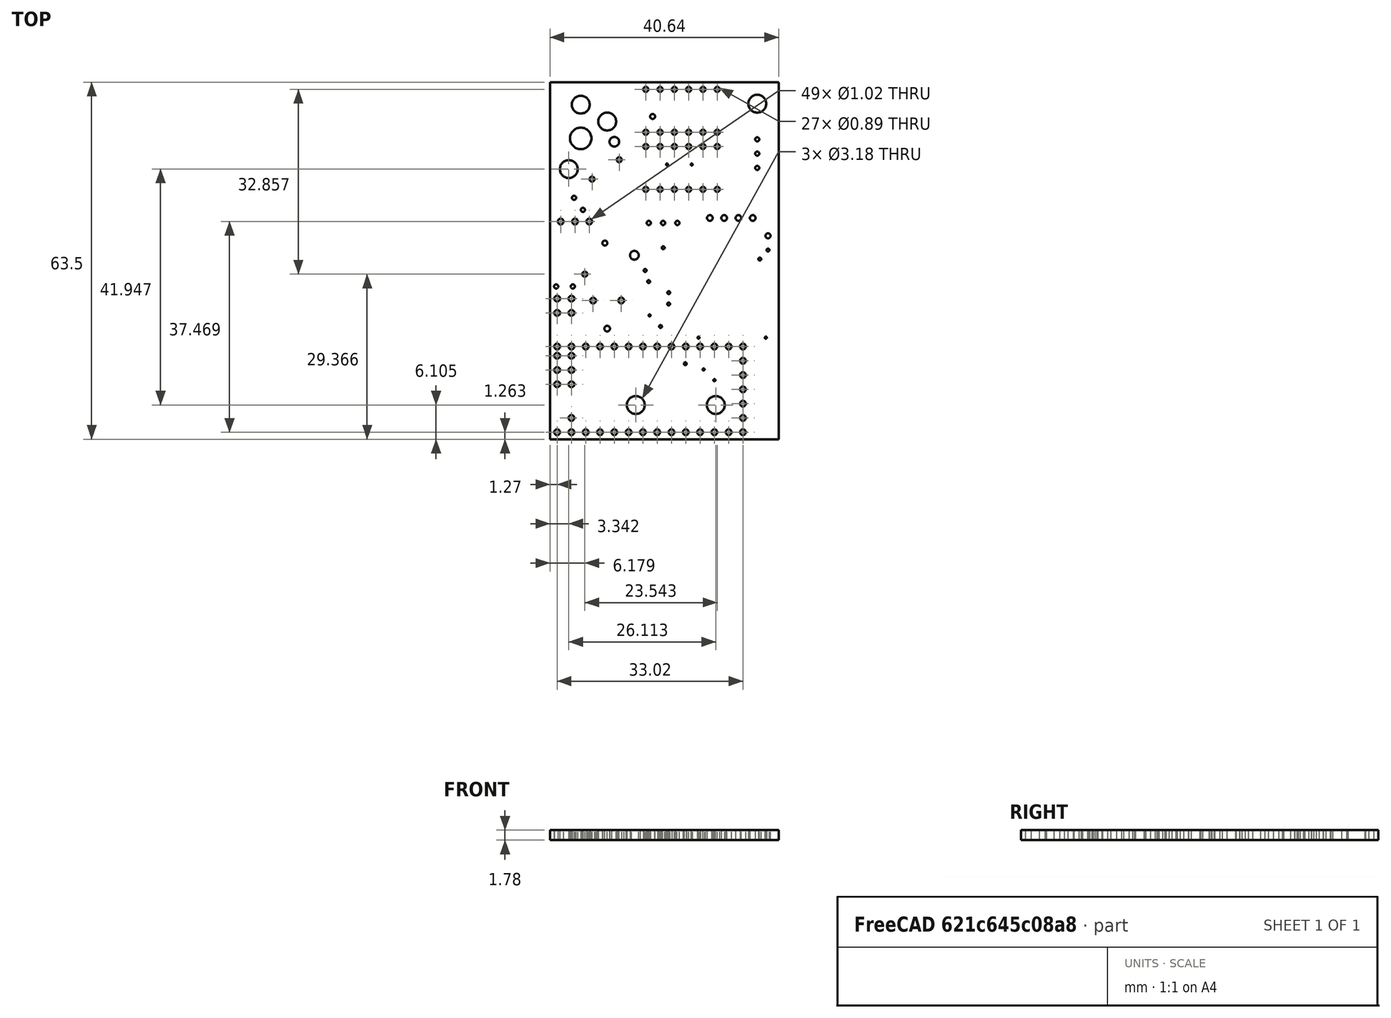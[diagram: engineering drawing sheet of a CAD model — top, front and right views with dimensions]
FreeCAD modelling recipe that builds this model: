
FCSTD DOCUMENT  (FreeCAD 1.0R39109 (Git))
Label: Version2PCB
License: All rights reserved
LicenseURL: https://en.wikipedia.org/wiki/All_rights_reserved
objects: Sketcher::SketchObject×2, PartDesign::Pad×1, PartDesign::Pocket×1, PartDesign::Body×1
note: 11 computed .brp shape members not serialized (recipe doc carries the construction recipe); baked Part::Feature solids carry a one-line shape summary decoded from their .brp

FEATURE [Sketcher::SketchObject] MainSketch
  ArcFitTolerance = 1e-06
  AttachmentSupport = -> [XY_Plane]
  FullyConstrained = false
  MakeInternals = false
  MapMode = 5
  sketch-geometry (4):
    g0: LineSegment StartX=0 StartY=0 StartZ=0 EndX=40.64 EndY=0 EndZ=0
    g1: LineSegment StartX=40.64 StartY=0 StartZ=0 EndX=40.64 EndY=63.5 EndZ=0
    g2: LineSegment StartX=40.64 StartY=63.5 StartZ=0 EndX=0 EndY=63.5 EndZ=0
    g3: LineSegment StartX=0 StartY=63.5 StartZ=0 EndX=0 EndY=0 EndZ=0
  constraints (4):
    c: Horizontal(g0)
    c: Horizontal(g2)
    c: Vertical(g1)
    c: Vertical(g3)
FEATURE [PartDesign::Pad] Main
  Direction = (0,0,1)
  Length = 1.778
  Length2 = 100.076
  Profile = -> MainSketch
  Refine = true
  Suppressed = false
  Type = 0
FEATURE [Sketcher::SketchObject] HoleSketch
  ArcFitTolerance = 1e-06
  AttachmentSupport = -> [XY_Plane]
  FullyConstrained = false
  MakeInternals = false
  MapMode = 5
  sketch-geometry (119):
    g0: Circle CenterX=5.4662 CenterY=59.5118 CenterZ=0 NormalX=0 NormalY=0 NormalZ=1 AngleXU=0 Radius=1.58564
    g1: Circle CenterX=5.45877 CenterY=53.5108 CenterZ=0 NormalX=0 NormalY=0 NormalZ=1 AngleXU=0 Radius=1.90871
    g2: Circle CenterX=10.16 CenterY=56.5113 CenterZ=0 NormalX=0 NormalY=0 NormalZ=1 AngleXU=0 Radius=1.58564
    g3: Circle CenterX=37.283 CenterY=32.0396 CenterZ=0 NormalX=0 NormalY=0 NormalZ=1 AngleXU=0 Radius=0.252515
    g4: Circle CenterX=19.6516 CenterY=20.0675 CenterZ=0 NormalX=0 NormalY=0 NormalZ=1 AngleXU=0 Radius=0.252515
    g5: Circle CenterX=38.7387 CenterY=33.6661 CenterZ=0 NormalX=0 NormalY=0 NormalZ=1 AngleXU=0 Radius=0.256228
    g6: Circle CenterX=20.1195 CenterY=34.0598 CenterZ=0 NormalX=0 NormalY=0 NormalZ=1 AngleXU=0 Radius=0.256228
    g7: Circle CenterX=21.1073 CenterY=26.0833 CenterZ=0 NormalX=0 NormalY=0 NormalZ=1 AngleXU=0 Radius=0.252515
    g8: Circle CenterX=21.0775 CenterY=24.0632 CenterZ=0 NormalX=0 NormalY=0 NormalZ=1 AngleXU=0 Radius=0.252515
    g9: Circle CenterX=17.0225 CenterY=62.2226 CenterZ=0 NormalX=0 NormalY=0 NormalZ=1 AngleXU=0 Radius=0.445614
    g10: Circle CenterX=17.0225 CenterY=54.6026 CenterZ=0 NormalX=0 NormalY=0 NormalZ=1 AngleXU=0 Radius=0.445614
    g11: Circle CenterX=19.5625 CenterY=62.2226 CenterZ=0 NormalX=0 NormalY=0 NormalZ=1 AngleXU=0 Radius=0.445614
    g12: Circle CenterX=19.5625 CenterY=54.6026 CenterZ=0 NormalX=0 NormalY=0 NormalZ=1 AngleXU=0 Radius=0.445614
    g13: Circle CenterX=22.1025 CenterY=62.2226 CenterZ=0 NormalX=0 NormalY=0 NormalZ=1 AngleXU=0 Radius=0.445614
    g14: Circle CenterX=22.1025 CenterY=54.6026 CenterZ=0 NormalX=0 NormalY=0 NormalZ=1 AngleXU=0 Radius=0.445614
    g15: Circle CenterX=24.6425 CenterY=62.2226 CenterZ=0 NormalX=0 NormalY=0 NormalZ=1 AngleXU=0 Radius=0.445614
    g16: Circle CenterX=24.6425 CenterY=54.6026 CenterZ=0 NormalX=0 NormalY=0 NormalZ=1 AngleXU=0 Radius=0.445614
    g17: Circle CenterX=27.1825 CenterY=62.2226 CenterZ=0 NormalX=0 NormalY=0 NormalZ=1 AngleXU=0 Radius=0.445614
    g18: Circle CenterX=29.7225 CenterY=62.2226 CenterZ=0 NormalX=0 NormalY=0 NormalZ=1 AngleXU=0 Radius=0.445614
    g19: Circle CenterX=27.1825 CenterY=54.6026 CenterZ=0 NormalX=0 NormalY=0 NormalZ=1 AngleXU=0 Radius=0.445614
    g20: Circle CenterX=29.7225 CenterY=54.6026 CenterZ=0 NormalX=0 NormalY=0 NormalZ=1 AngleXU=0 Radius=0.445614
    g21: Circle CenterX=34.29 CenterY=1.26257 CenterZ=0 NormalX=0 NormalY=0 NormalZ=1 AngleXU=0 Radius=0.508743
    g22: Circle CenterX=31.75 CenterY=1.26257 CenterZ=0 NormalX=0 NormalY=0 NormalZ=1 AngleXU=0 Radius=0.508743
    g23: Circle CenterX=29.21 CenterY=1.26257 CenterZ=0 NormalX=0 NormalY=0 NormalZ=1 AngleXU=0 Radius=0.508743
    g24: Circle CenterX=34.29 CenterY=16.5026 CenterZ=0 NormalX=0 NormalY=0 NormalZ=1 AngleXU=0 Radius=0.508743
    g25: Circle CenterX=34.29 CenterY=3.80257 CenterZ=0 NormalX=0 NormalY=0 NormalZ=1 AngleXU=0 Radius=0.508743
    g26: Circle CenterX=34.29 CenterY=6.34257 CenterZ=0 NormalX=0 NormalY=0 NormalZ=1 AngleXU=0 Radius=0.508743
    g27: Circle CenterX=34.29 CenterY=8.88257 CenterZ=0 NormalX=0 NormalY=0 NormalZ=1 AngleXU=0 Radius=0.508743
    g28: Circle CenterX=34.29 CenterY=11.4226 CenterZ=0 NormalX=0 NormalY=0 NormalZ=1 AngleXU=0 Radius=0.508743
    g29: Circle CenterX=34.29 CenterY=13.9626 CenterZ=0 NormalX=0 NormalY=0 NormalZ=1 AngleXU=0 Radius=0.508743
    g30: Circle CenterX=26.67 CenterY=1.26257 CenterZ=0 NormalX=0 NormalY=0 NormalZ=1 AngleXU=0 Radius=0.508743
    g31: Circle CenterX=24.13 CenterY=1.26257 CenterZ=0 NormalX=0 NormalY=0 NormalZ=1 AngleXU=0 Radius=0.508743
    g32: Circle CenterX=21.59 CenterY=1.26257 CenterZ=0 NormalX=0 NormalY=0 NormalZ=1 AngleXU=0 Radius=0.508743
    g33: Circle CenterX=19.05 CenterY=1.26257 CenterZ=0 NormalX=0 NormalY=0 NormalZ=1 AngleXU=0 Radius=0.508743
    g34: Circle CenterX=16.51 CenterY=1.26257 CenterZ=0 NormalX=0 NormalY=0 NormalZ=1 AngleXU=0 Radius=0.508743
    g35: Circle CenterX=13.97 CenterY=1.26257 CenterZ=0 NormalX=0 NormalY=0 NormalZ=1 AngleXU=0 Radius=0.508743
    g36: Circle CenterX=11.43 CenterY=1.26257 CenterZ=0 NormalX=0 NormalY=0 NormalZ=1 AngleXU=0 Radius=0.508743
    g37: Circle CenterX=8.89 CenterY=1.26257 CenterZ=0 NormalX=0 NormalY=0 NormalZ=1 AngleXU=0 Radius=0.508743
    g38: Circle CenterX=6.35 CenterY=1.26257 CenterZ=0 NormalX=0 NormalY=0 NormalZ=1 AngleXU=0 Radius=0.508743
    g39: Circle CenterX=3.81 CenterY=1.26257 CenterZ=0 NormalX=0 NormalY=0 NormalZ=1 AngleXU=0 Radius=0.508743
    g40: Circle CenterX=1.27 CenterY=1.26257 CenterZ=0 NormalX=0 NormalY=0 NormalZ=1 AngleXU=0 Radius=0.508743
    g41: Circle CenterX=31.75 CenterY=16.5026 CenterZ=0 NormalX=0 NormalY=0 NormalZ=1 AngleXU=0 Radius=0.508743
    g42: Circle CenterX=29.21 CenterY=16.5026 CenterZ=0 NormalX=0 NormalY=0 NormalZ=1 AngleXU=0 Radius=0.508743
    g43: Circle CenterX=26.67 CenterY=16.5026 CenterZ=0 NormalX=0 NormalY=0 NormalZ=1 AngleXU=0 Radius=0.508743
    g44: Circle CenterX=24.13 CenterY=16.5026 CenterZ=0 NormalX=0 NormalY=0 NormalZ=1 AngleXU=0 Radius=0.508743
    g45: Circle CenterX=21.59 CenterY=16.5026 CenterZ=0 NormalX=0 NormalY=0 NormalZ=1 AngleXU=0 Radius=0.508743
    g46: Circle CenterX=19.05 CenterY=16.5026 CenterZ=0 NormalX=0 NormalY=0 NormalZ=1 AngleXU=0 Radius=0.508743
    g47: Circle CenterX=16.51 CenterY=16.5026 CenterZ=0 NormalX=0 NormalY=0 NormalZ=1 AngleXU=0 Radius=0.508743
    g48: Circle CenterX=13.97 CenterY=16.5026 CenterZ=0 NormalX=0 NormalY=0 NormalZ=1 AngleXU=0 Radius=0.508743
    g49: Circle CenterX=11.43 CenterY=16.5026 CenterZ=0 NormalX=0 NormalY=0 NormalZ=1 AngleXU=0 Radius=0.508743
    g50: Circle CenterX=8.89 CenterY=16.5026 CenterZ=0 NormalX=0 NormalY=0 NormalZ=1 AngleXU=0 Radius=0.508743
    g51: Circle CenterX=6.35 CenterY=16.5026 CenterZ=0 NormalX=0 NormalY=0 NormalZ=1 AngleXU=0 Radius=0.508743
    g52: Circle CenterX=3.81 CenterY=16.5026 CenterZ=0 NormalX=0 NormalY=0 NormalZ=1 AngleXU=0 Radius=0.508743
    g53: Circle CenterX=1.27 CenterY=16.5026 CenterZ=0 NormalX=0 NormalY=0 NormalZ=1 AngleXU=0 Radius=0.508743
    g54: Circle CenterX=3.81 CenterY=3.80257 CenterZ=0 NormalX=0 NormalY=0 NormalZ=1 AngleXU=0 Radius=0.508743
    g55: Circle CenterX=15.24 CenterY=6.10491 CenterZ=0 NormalX=0 NormalY=0 NormalZ=1 AngleXU=0 Radius=1.58936
    g56: Circle CenterX=36.83 CenterY=59.6826 CenterZ=0 NormalX=0 NormalY=0 NormalZ=1 AngleXU=0 Radius=1.58564
    g57: Circle CenterX=29.4551 CenterY=6.10491 CenterZ=0 NormalX=0 NormalY=0 NormalZ=1 AngleXU=0 Radius=1.58936
    g58: Circle CenterX=1.27 CenterY=12.3212 CenterZ=0 NormalX=0 NormalY=0 NormalZ=1 AngleXU=0 Radius=0.512456
    g59: Circle CenterX=1.27 CenterY=9.78123 CenterZ=0 NormalX=0 NormalY=0 NormalZ=1 AngleXU=0 Radius=0.512456
    g60: Circle CenterX=3.81 CenterY=9.78123 CenterZ=0 NormalX=0 NormalY=0 NormalZ=1 AngleXU=0 Radius=0.512456
    g61: Circle CenterX=1.27 CenterY=14.8612 CenterZ=0 NormalX=0 NormalY=0 NormalZ=1 AngleXU=0 Radius=0.512456
    g62: Circle CenterX=3.81 CenterY=12.3212 CenterZ=0 NormalX=0 NormalY=0 NormalZ=1 AngleXU=0 Radius=0.512456
    g63: Circle CenterX=3.81 CenterY=14.8612 CenterZ=0 NormalX=0 NormalY=0 NormalZ=1 AngleXU=0 Radius=0.512456
    g64: Circle CenterX=10.16 CenterY=19.6813 CenterZ=0 NormalX=0 NormalY=0 NormalZ=1 AngleXU=0 Radius=0.505029
    g65: Circle CenterX=7.66456 CenterY=24.6796 CenterZ=0 NormalX=0 NormalY=0 NormalZ=1 AngleXU=0 Radius=0.508743
    g66: Circle CenterX=12.6629 CenterY=24.6796 CenterZ=0 NormalX=0 NormalY=0 NormalZ=1 AngleXU=0 Radius=0.512456
    g67: Circle CenterX=1.27 CenterY=22.4812 CenterZ=0 NormalX=0 NormalY=0 NormalZ=1 AngleXU=0 Radius=0.512456
    g68: Circle CenterX=3.81 CenterY=22.4812 CenterZ=0 NormalX=0 NormalY=0 NormalZ=1 AngleXU=0 Radius=0.512456
    g69: Circle CenterX=1.27 CenterY=25.0212 CenterZ=0 NormalX=0 NormalY=0 NormalZ=1 AngleXU=0 Radius=0.512456
    g70: Circle CenterX=3.81 CenterY=25.0212 CenterZ=0 NormalX=0 NormalY=0 NormalZ=1 AngleXU=0 Radius=0.512456
    g71: Circle CenterX=1.90129 CenterY=38.7313 CenterZ=0 NormalX=0 NormalY=0 NormalZ=1 AngleXU=0 Radius=0.508743
    g72: Circle CenterX=6.98129 CenterY=38.7313 CenterZ=0 NormalX=0 NormalY=0 NormalZ=1 AngleXU=0 Radius=0.508743
    g73: Circle CenterX=4.44129 CenterY=38.7313 CenterZ=0 NormalX=0 NormalY=0 NormalZ=1 AngleXU=0 Radius=0.508743
    g74: Circle CenterX=3.34211 CenterY=48.052 CenterZ=0 NormalX=0 NormalY=0 NormalZ=1 AngleXU=0 Radius=1.58936
    g75: Circle CenterX=36.83 CenterY=48.26 CenterZ=0 NormalX=0 NormalY=0 NormalZ=1 AngleXU=0 Radius=0.367632
    g76: Circle CenterX=36.83 CenterY=53.34 CenterZ=0 NormalX=0 NormalY=0 NormalZ=1 AngleXU=0 Radius=0.367632
    g77: Circle CenterX=36.83 CenterY=50.8 CenterZ=0 NormalX=0 NormalY=0 NormalZ=1 AngleXU=0 Radius=0.367632
    g78: Circle CenterX=17.5498 CenterY=38.4713 CenterZ=0 NormalX=0 NormalY=0 NormalZ=1 AngleXU=0 Radius=0.367632
    g79: Circle CenterX=22.6298 CenterY=38.4713 CenterZ=0 NormalX=0 NormalY=0 NormalZ=1 AngleXU=0 Radius=0.367632
    g80: Circle CenterX=20.0898 CenterY=38.4713 CenterZ=0 NormalX=0 NormalY=0 NormalZ=1 AngleXU=0 Radius=0.367632
    g81: Circle CenterX=36.0353 CenterY=39.3626 CenterZ=0 NormalX=0 NormalY=0 NormalZ=1 AngleXU=0 Radius=0.505029
    g82: Circle CenterX=33.4953 CenterY=39.3626 CenterZ=0 NormalX=0 NormalY=0 NormalZ=1 AngleXU=0 Radius=0.505029
    g83: Circle CenterX=30.9553 CenterY=39.3626 CenterZ=0 NormalX=0 NormalY=0 NormalZ=1 AngleXU=0 Radius=0.505029
    g84: Circle CenterX=28.4153 CenterY=39.3626 CenterZ=0 NormalX=0 NormalY=0 NormalZ=1 AngleXU=0 Radius=0.505029
    g85: Circle CenterX=17.5275 CenterY=28.044 CenterZ=0 NormalX=0 NormalY=0 NormalZ=1 AngleXU=0 Radius=0.252515
    g86: Circle CenterX=38.7387 CenterY=36.1913 CenterZ=0 NormalX=0 NormalY=0 NormalZ=1 AngleXU=0 Radius=0.441901
    g87: Circle CenterX=17.0225 CenterY=52.0626 CenterZ=0 NormalX=0 NormalY=0 NormalZ=1 AngleXU=0 Radius=0.445614
    g88: Circle CenterX=17.0225 CenterY=44.4426 CenterZ=0 NormalX=0 NormalY=0 NormalZ=1 AngleXU=0 Radius=0.445614
    g89: Circle CenterX=19.5625 CenterY=52.0626 CenterZ=0 NormalX=0 NormalY=0 NormalZ=1 AngleXU=0 Radius=0.445614
    g90: Circle CenterX=19.5625 CenterY=44.4426 CenterZ=0 NormalX=0 NormalY=0 NormalZ=1 AngleXU=0 Radius=0.445614
    g91: Circle CenterX=22.1025 CenterY=52.0626 CenterZ=0 NormalX=0 NormalY=0 NormalZ=1 AngleXU=0 Radius=0.445614
    g92: Circle CenterX=22.1025 CenterY=44.4426 CenterZ=0 NormalX=0 NormalY=0 NormalZ=1 AngleXU=0 Radius=0.445614
    g93: Circle CenterX=24.6425 CenterY=52.0626 CenterZ=0 NormalX=0 NormalY=0 NormalZ=1 AngleXU=0 Radius=0.445614
    g94: Circle CenterX=24.6425 CenterY=44.4426 CenterZ=0 NormalX=0 NormalY=0 NormalZ=1 AngleXU=0 Radius=0.445614
    g95: Circle CenterX=27.1825 CenterY=52.0626 CenterZ=0 NormalX=0 NormalY=0 NormalZ=1 AngleXU=0 Radius=0.445614
    g96: Circle CenterX=29.7225 CenterY=52.0626 CenterZ=0 NormalX=0 NormalY=0 NormalZ=1 AngleXU=0 Radius=0.445614
    g97: Circle CenterX=27.1825 CenterY=44.4426 CenterZ=0 NormalX=0 NormalY=0 NormalZ=1 AngleXU=0 Radius=0.445614
    g98: Circle CenterX=29.7225 CenterY=44.4426 CenterZ=0 NormalX=0 NormalY=0 NormalZ=1 AngleXU=0 Radius=0.445614
    g99: Circle CenterX=26.3952 CenterY=18.0771 CenterZ=0 NormalX=0 NormalY=0 NormalZ=1 AngleXU=0 Radius=0.178246
    g100: Circle CenterX=38.3525 CenterY=18.0771 CenterZ=0 NormalX=0 NormalY=0 NormalZ=1 AngleXU=0 Radius=0.178246
    g101: Circle CenterX=17.6909 CenterY=22.0282 CenterZ=0 NormalX=0 NormalY=0 NormalZ=1 AngleXU=0 Radius=0.178246
    g102: Circle CenterX=27.3013 CenterY=12.4178 CenterZ=0 NormalX=0 NormalY=0 NormalZ=1 AngleXU=0 Radius=0.178246
    g103: Circle CenterX=29.2174 CenterY=10.5165 CenterZ=0 NormalX=0 NormalY=0 NormalZ=1 AngleXU=0 Radius=0.178246
    g104: Circle CenterX=1.09175 CenterY=27.1825 CenterZ=0 NormalX=0 NormalY=0 NormalZ=1 AngleXU=0 Radius=0.367632
    g105: Circle CenterX=4.05509 CenterY=27.1825 CenterZ=0 NormalX=0 NormalY=0 NormalZ=1 AngleXU=0 Radius=0.371345
    g106: Circle CenterX=14.9875 CenterY=32.7304 CenterZ=0 NormalX=0 NormalY=0 NormalZ=1 AngleXU=0 Radius=0.776111
    g107: Circle CenterX=11.43 CenterY=52.9167 CenterZ=0 NormalX=0 NormalY=0 NormalZ=1 AngleXU=0 Radius=0.854094
    g108: Circle CenterX=20.7953 CenterY=48.869 CenterZ=0 NormalX=0 NormalY=0 NormalZ=1 AngleXU=0 Radius=0.178246
    g109: Circle CenterX=25.1772 CenterY=48.869 CenterZ=0 NormalX=0 NormalY=0 NormalZ=1 AngleXU=0 Radius=0.178246
    g110: Circle CenterX=12.2989 CenterY=49.7157 CenterZ=0 NormalX=0 NormalY=0 NormalZ=1 AngleXU=0 Radius=0.445614
    g111: Circle CenterX=7.47146 CenterY=46.2696 CenterZ=0 NormalX=0 NormalY=0 NormalZ=1 AngleXU=0 Radius=0.445614
    g112: Circle CenterX=6.17918 CenterY=29.366 CenterZ=0 NormalX=0 NormalY=0 NormalZ=1 AngleXU=0 Radius=0.445614
    g113: Circle CenterX=9.75152 CenterY=34.8916 CenterZ=0 NormalX=0 NormalY=0 NormalZ=1 AngleXU=0 Radius=0.441901
    g114: Circle CenterX=4.27789 CenterY=42.9423 CenterZ=0 NormalX=0 NormalY=0 NormalZ=1 AngleXU=0 Radius=0.371345
    g115: Circle CenterX=5.84497 CenterY=40.8034 CenterZ=0 NormalX=0 NormalY=0 NormalZ=1 AngleXU=0 Radius=0.367632
    g116: Circle CenterX=18.233 CenterY=57.4099 CenterZ=0 NormalX=0 NormalY=0 NormalZ=1 AngleXU=0 Radius=0.441901
    g117: Circle CenterX=16.9036 CenterY=30.0195 CenterZ=0 NormalX=0 NormalY=0 NormalZ=1 AngleXU=0 Radius=0.252515
    g118: Circle CenterX=24.0483 CenterY=13.4427 CenterZ=0 NormalX=0 NormalY=0 NormalZ=1 AngleXU=0 Radius=0.252515
FEATURE [PartDesign::Pocket] Holes
  BaseFeature = -> Main
  Direction = (0,0,-1)
  Length = 3.556
  Length2 = 5
  Profile = -> HoleSketch
  Refine = true
  Reversed = true
  Suppressed = false
  Type = 0
FEATURE [PartDesign::Body] Body
  AllowCompound = false
  Group = -> [MainSketch,Main,HoleSketch,Holes]
  Origin = -> Origin
  Tip = -> Holes
